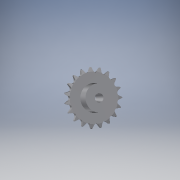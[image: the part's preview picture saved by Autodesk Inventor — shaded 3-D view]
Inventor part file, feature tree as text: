
AUTODESK INVENTOR PART (.ipt)
format: ipt  version: 2018 (Build 220112000, 112)  size: 283,648 bytes
history: native  units: mm (DEFAULTED — no unit token found)
features: sketch x5, extrude x4, chamfer x2, other x1, pattern_circular x1, plane x1
ambient origin geometry x8: Origin, YZ Plane, XZ Plane, XY Plane, X Axis, Y Axis, Z Axis, Center Point
bodies: Solid1 (feature_tree)
feature tree (14):
  extrude  "Extrusion1"  Depth=17.0mm TaperAngle=0.0deg
  sketch  "Sketch2"  dims[d3=83.7184mm d4=63.5mm]
  sketch  "Sketch3"  dims[d5=10.9601mm]
  extrude  "Sprocket Disc"  Depth=63.5mm
  other  "Work Axis1"
  chamfer  "Sprocket Chamfer 1"  Distance=1.8288mm
  chamfer  "Sprocket Chamfer 2"  Distance=3.8862mm
  extrude  "Tooth Cut"  Depth=6.5532mm
  pattern_circular  "Tooth Cut Array"  [2 undecoded]
  extrude  "TaperBore"  Depth=10.0mm
  sketch  "Sketch5"  dims[d7=1.8288mm d8=1.8288mm d9=3.8862mm d10=6.5532mm d11=6.5532mm d12=50.0mm d13=1.190625mm d14=1.190625mm d15=6.35mm d16=5.0mm d17=7.2136mm d19=6.0mm d20=0.0mm d21=41.8592mm d22=7.2136mm d23=0.0mm d25=190.0mm d27=360.0deg d28=1.190625mm d29=6.35mm d30=6.35mm d31=1.190625mm d32=12.7mm d33=10.0mm d34=-0.698132mm d35=16.580628mm d36=16.580628mm d37=44.45mm d56=45.0deg d57=45.0deg]
  plane  "Work Plane3"
  sketch  "Sketch1"  dims[d0=35.0mm d1=17.0mm d2=0.0mm]
  sketch  "Sketch4"  dims[d6=10.9601mm]
note: 2 required parameter values undecoded (feature->parameter linkage not recoverable at this tier; creation-order binding heuristic only, values carry confidence <= 0.55)
